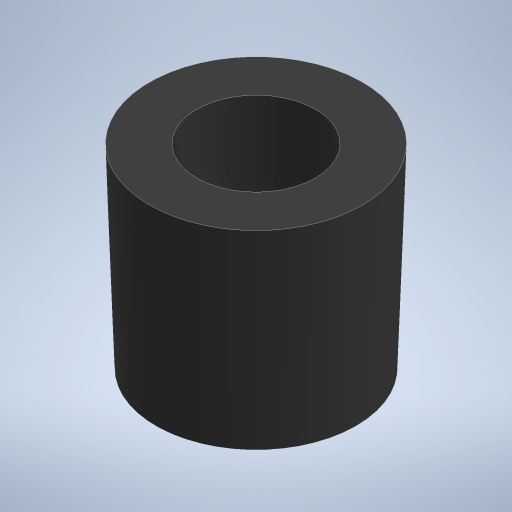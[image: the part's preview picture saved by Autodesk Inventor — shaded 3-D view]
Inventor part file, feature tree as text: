
AUTODESK INVENTOR PART (.ipt)
format: ipt  version: 2023.1 (Build 271208000, 208)  size: 213,504 bytes
history: native  units: mm
features: sketch x2, revolve x1, hole x1
ambient origin geometry x8: Origin, YZ Plane, XZ Plane, XY Plane, X Axis, Y Axis, Z Axis, Center Point
bodies: Solid1 (feature_tree)
feature tree (4):
  revolve  "Revolution1"  [1 undecoded]
  hole  "Hole1"  [1 undecoded]
  sketch  "Sketch1"  dims[d0=9.85mm d1=9.25mm]
  sketch  "Sketch2"  dims[d2=18.0mm d3=90.0deg d4=9.28mm d5=11.0mm d6=6.0mm d7=4.0mm d8=2.0mm d9=90.0deg d10=12.5mm d11=20.594885mm]
note: 2 required parameter values undecoded (feature->parameter linkage not recoverable at this tier; creation-order binding heuristic only, values carry confidence <= 0.55)